# Revit family: Legrand_Gestion_eclairage_Detecteur_Presence_Plafond_DALI
name_source: partatom
category: Dispositifs d'éclairage
units: mm (PartAtom-declared; Revit-internal decimal feet)

## family parameters
Conserver l'orientation des annotations = Non
Cote de connecteur circulaire = Utiliser le diamètre
Couper avec des vides une fois chargée = Non
Hôte = Face
Partagée = Non
Point de calcul de pièce = Non
Type d'élément = Normal

## types (2) — shared parameters
Adapté pour transmission sans fil = Oui
Angle de détection horizontal (MAX) (°) = 360
Angle de détection horizontal (MIN) (°) = 360
Collecteur de terre = Non
Condition Générale d'Utilisation = https://export.legrand.com
Cosses d'artère secondaire = Non
Couleur = Blanc
Coupure forcée = Oui
Durée d'enclenchement max. (mn) = 30
Durée d'enclenchement min. (s) = 5
Elévation par défaut = 1219 mm
Entrée secondaire = Non
Exécution - Modèle = détecteur de présence
Fabricant = Legrand
Fonction variateur intégré = Oui
Fréquence (MAX) (Hz) = 60
Fréquence (MIN) (Hz) = 50
Gestion CVC = Non
Gestion alarme = Non
Hauteur de montage maximale (m) = 2.5
Liaison neutre = Non
Mode de montage = encastré
Numéro RAL = 9006
Réglage de lumière constante = Oui
Sensibilité lumineuse réglable = Oui
Sensibilité réglable = Oui
Température (MAX) (°C) = 45
Température (MIN) (°C) = -5
Tension nominale (V) = 16
Télécommandable = Oui
URL = http://www.legrandoc.com
zero-valued in all types: Capacité de coupure max. (W), Courant de démarrage max. (A), Sensibilité lumineuse (MAX) (lx), Sensibilité lumineuse (MIN) (lx)

## per-type parameters (varying)
| type | COULOIR | Classe de protection (IP) | DUAL-TECH | Description | Diamètre de détection sur le plancher (m) | Modèle | Portée max. frontale (m) | Portée max. latérale (m) |
| COULOIR | Oui | IP41 | Non | Ecodétecteur DALI spécial couloir - IP 41 - montage faux-plafond | 12 | 048936 | 12 | 12 |
| DUAL-TECH | Non | IP20 | Oui | Ecodétecteur DALI spécial espace de travail - IP 20 - montage faux-plafond | 8 | 048935 | 8 | 8 |
